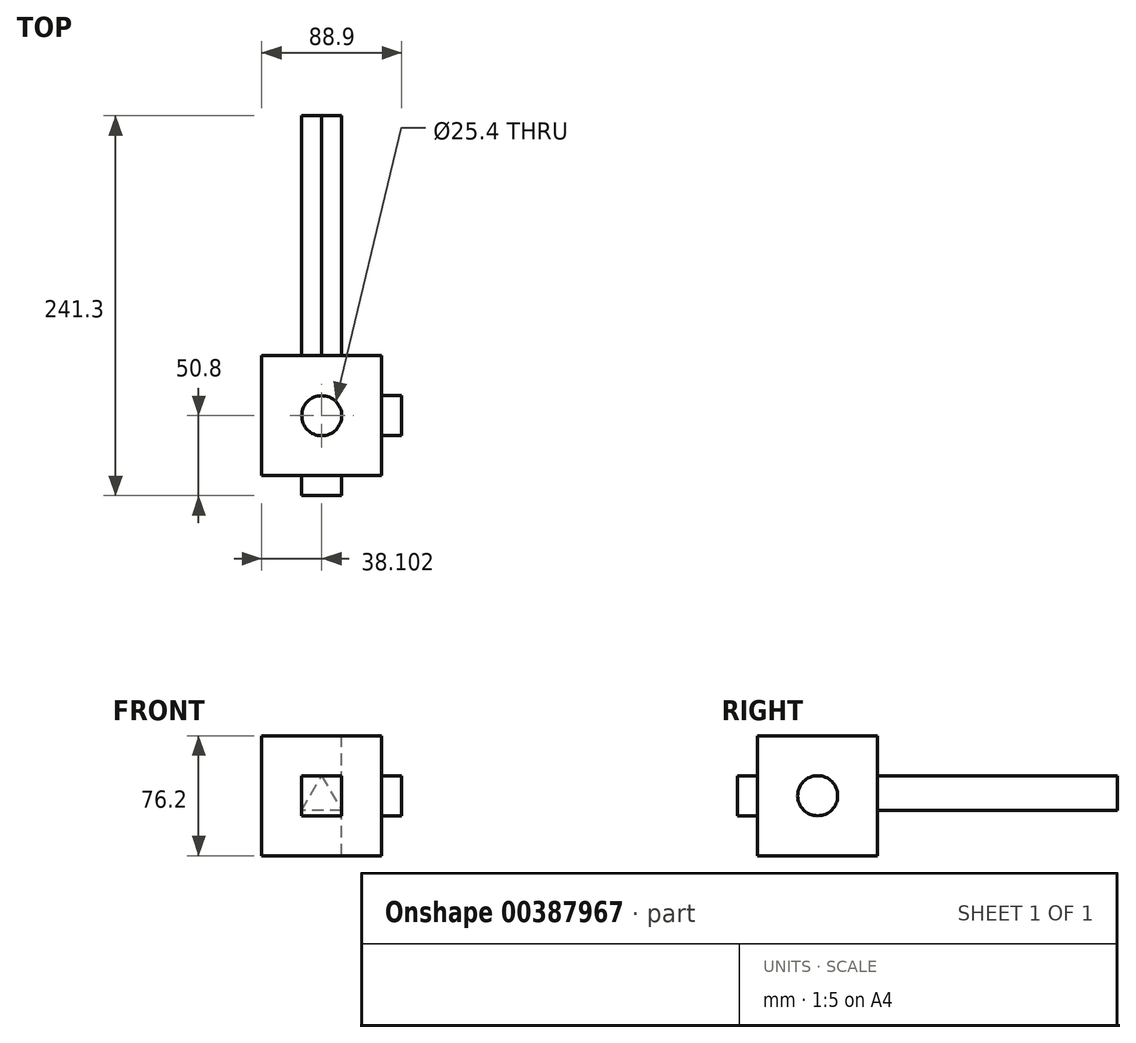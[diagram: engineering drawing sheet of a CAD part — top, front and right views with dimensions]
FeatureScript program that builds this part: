
annotation { "Feature Type Name" : "Feature", "Feature Type Description" : "" }
export const myFeature = defineFeature(function(context is Context, id is Id, definition is map)
    precondition{}
    {
        {
            var Q0;
            Q0=qCreatedBy(makeId("Front.planeOp"),FACE);
            var sketch = newSketch(context, id + "F0", { "sketchPlane" : qUnion([Q0])});
            skLineSegment(sketch, "E0.bottom", {"start": v(-38.86, 38.94) * mm, "end": v(37.34, 38.94) * mm});
            skLineSegment(sketch, "E0.top", {"start": v(-38.86, -37.26) * mm, "end": v(37.34, -37.26) * mm});
            skLineSegment(sketch, "E0.left", {"start": v(-38.86, 38.94) * mm, "end": v(-38.86, -37.26) * mm});
            skLineSegment(sketch, "E0.right", {"start": v(37.34, 38.94) * mm, "end": v(37.34, -37.26) * mm});
            skSolve(sketch);
        }
        {
            var Q0;
            Q0 = qSketchRegion(id + "F0", true);
            extrude(context, id + "F1", {"entities" : qUnion([Q0]), "depth" : 76.2 * mm});
        }
        {
            var Q0;
            Q0=makeQuery(id+"F1.opExtrude","SWEPT_FACE",FACE,{"disambiguationData":[OSD([sQuery(id+"F0.wireOp",EDGE,"E0.bottom")])]});
            var sketch = newSketch(context, id + "F2", { "sketchPlane" : qUnion([Q0])});
            skPoint(sketch, "E1", {"position": v(-0.76, -38.1) * mm});
            skSolve(sketch);
        }
        {
            var Q0;
            Q0=sQuery(id+"F2.wireOp",VERTEX,"E1");
            var Q1;
            Q1=makeQuery(id+"F1.opExtrude","SWEPT_BODY",BODY,{"disambiguationData":[OSD([sQuery(id+"F0.wireOp",EDGE,"E0.bottom"),sQuery(id+"F0.wireOp",EDGE,"E0.top"),sQuery(id+"F0.wireOp",EDGE,"E0.left"),sQuery(id+"F0.wireOp",EDGE,"E0.right")])]});
            hole(context, id + "F3", {"style" : HoleStyle.SIMPLE, "endStyle" : HoleEndStyle.THROUGH, "holeDiameter" : 25.4 * mm, "isTappedThrough" : true, "tappedDepth" : 12.7 * mm, "tapClearance" : 3, "locations" : qUnion([Q0]), "scope" : qUnion([Q1])});
        }
        {
            var Q0;
            Q0=makeQuery(id+"F1.opExtrude","CAP_FACE",FACE,{"disambiguationData":[OSD([sQuery(id+"F0.wireOp",EDGE,"E0.bottom"),sQuery(id+"F0.wireOp",EDGE,"E0.top"),sQuery(id+"F0.wireOp",EDGE,"E0.left"),sQuery(id+"F0.wireOp",EDGE,"E0.right")])],"isStart":false});
            var sketch = newSketch(context, id + "F4", { "sketchPlane" : qUnion([Q0])});
            skLineSegment(sketch, "E2.bottom", {"start": v(-13.46, -11.86) * mm, "end": v(11.94, -11.86) * mm});
            skLineSegment(sketch, "E2.top", {"start": v(-13.46, 13.54) * mm, "end": v(11.94, 13.54) * mm});
            skLineSegment(sketch, "E2.left", {"start": v(-13.46, -11.86) * mm, "end": v(-13.46, 13.54) * mm});
            skLineSegment(sketch, "E2.right", {"start": v(11.94, -11.86) * mm, "end": v(11.94, 13.54) * mm});
            skSolve(sketch);
        }
        {
            var Q0;
            Q0=makeQuery(id+"F4.imprint","IMPRINT",FACE,{"disambiguationData":[TD([[makeQuery(id+"F4.imprint","IMPRINT",EDGE,{"derivedFrom":sQuery(id+"F4.wireOp",EDGE,"E2.bottom")}),1.0]])]});
            extrude(context, id + "F5", {"entities" : qUnion([Q0]), "operationType" : NewBodyOperationType.ADD, "depth" : 12.7 * mm});
        }
        {
            var Q0;
            Q0=makeQuery(id+"F1.opExtrude","SWEPT_FACE",FACE,{"disambiguationData":[OSD([sQuery(id+"F0.wireOp",EDGE,"E0.right")])]});
            var sketch = newSketch(context, id + "F6", { "sketchPlane" : qUnion([Q0])});
            skPoint(sketch, "E3", {"position": v(-38.1, 0.84) * mm});
            skCircle(sketch, "E4", {"center": v(-38.1, 0.84) * mm, "radius": 12.7 * mm});
            skSolve(sketch);
        }
        {
            var Q0;
            Q0=makeQuery(id+"F6.imprint","IMPRINT",FACE,{"disambiguationData":[TD([[makeQuery(id+"F6.imprint","IMPRINT",EDGE,{"derivedFrom":sQuery(id+"F6.wireOp",EDGE,"E4")}),1.0]])]});
            extrude(context, id + "F7", {"entities" : qUnion([Q0]), "operationType" : NewBodyOperationType.ADD, "depth" : 12.7 * mm});
        }
        {
            var Q0;
            Q0=makeQuery(id+"F1.opExtrude","CAP_FACE",FACE,{"disambiguationData":[OSD([sQuery(id+"F0.wireOp",EDGE,"E0.bottom"),sQuery(id+"F0.wireOp",EDGE,"E0.top"),sQuery(id+"F0.wireOp",EDGE,"E0.left"),sQuery(id+"F0.wireOp",EDGE,"E0.right")])],"isStart":true});
            var sketch = newSketch(context, id + "F8", { "sketchPlane" : qUnion([Q0])});
            skLineSegment(sketch, "E5", {"start": v(0.76, 13.54) * mm, "end": v(-11.94, -8.46) * mm});
            skLineSegment(sketch, "E6", {"start": v(-11.94, -8.46) * mm, "end": v(13.46, -8.46) * mm});
            skLineSegment(sketch, "E7", {"start": v(13.46, -8.46) * mm, "end": v(0.76, 13.54) * mm});
            skSolve(sketch);
        }
        {
            var Q0;
            Q0=makeQuery(id+"F8.imprint","IMPRINT",FACE,{"disambiguationData":[TD([[makeQuery(id+"F8.imprint","IMPRINT",EDGE,{"derivedFrom":sQuery(id+"F8.wireOp",EDGE,"E5")}),1.0]])]});
            extrude(context, id + "F9", {"entities" : qUnion([Q0]), "operationType" : NewBodyOperationType.ADD, "depth" : 152.4 * mm});
        }
    });
